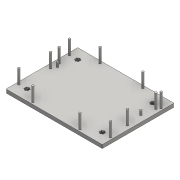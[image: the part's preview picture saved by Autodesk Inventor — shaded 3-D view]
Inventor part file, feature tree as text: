
AUTODESK INVENTOR PART (.ipt)
format: ipt  version: 2016 (Build 200138000, 138)  size: 360,448 bytes
history: native  units: mm
features: extrude x6, sketch x2, hole x2, other x2, fillet x2, pattern_linear x1
ambient origin geometry x8: Origin, YZ Plane, XZ Plane, XY Plane, X Axis, Y Axis, Z Axis, Center Point
bodies: Solid1 (feature_tree)
feature tree (15):
  sketch  "Sketch1"  dims[d9=60.0mm d10=5.0mm]
  hole  "HOLES1"  [1 undecoded]
  other  "OUTLINE1"
  other  "OUTLINE2"
  extrude  "Extrusion2"  Depth=5.0mm TaperAngle=0.0deg
  fillet  "Fillet1"  Radius=0.5mm
  extrude  "Extrusion7"  Depth=6.0mm
  fillet  "Fillet3"  Radius=3.0mm
  extrude  "Extrusion8"  Depth=6.0mm
  extrude  "Extrusion9"  Depth=6.0mm
  pattern_linear  "Rectangular Pattern2"  Spacing1=3.0mm  [1 undecoded]
  sketch  "Sketch8"  dims[d11=5.0mm d14=5.0mm d15=0.0mm d36=0.5mm d44=3.0mm d45=3.0mm d46=3.0mm d47=3.0mm d48=3.0mm d49=3.0mm d50=3.0mm d51=3.0mm d52=10.0mm d53=10.0mm d56=10.0mm d57=10.0mm d58=0.0mm d59=0.5mm d62=5.0mm d63=2.85mm d64=1.0mm d65=60.0mm d67=360.0deg d69=2.3mm d70=0.0mm d71=5.0mm d72=10.0mm d73=0.0mm d74=20.0mm d76=72.0mm d77=20.0mm d79=107.0mm d80=3.0mm d81=30.0mm d82=1.8mm d83=3.0mm d84=30.0mm d85=1.8mm d86=3.0mm d87=3.0mm d88=3.0mm d90=3.0mm d91=3.0mm d92=3.0mm d93=3.0mm d94=3.0mm d95=3.0mm d96=3.0mm d97=1.8mm d98=10.0mm d99=1.8mm d100=10.0mm d101=1.8mm d102=5.0mm d103=1.8mm d104=5.0mm d105=3.0mm d106=1.8mm d107=33.0mm d108=1.8mm d109=5.0mm d110=1.8mm d111=5.0mm d112=1.8mm d113=10.0mm d114=1.8mm d115=30.0mm d116=1.8mm d117=30.0mm d118=1.8mm d119=10.0mm d120=3.0mm d121=1.8mm d122=33.0mm d123=3.0mm d124=6.0mm d125=4.0mm d126=2.0mm d127=90.0deg d128=8.0mm d129=20.594885mm d130=20.0mm d131=0.0mm d132=6.0mm d133=0.0mm]
  hole  "Hole1"  [1 undecoded]
  extrude  "Extrusion10"  Depth=6.0mm
  extrude  "Extrusion11"  Depth=6.0mm
note: 3 required parameter values undecoded (feature->parameter linkage not recoverable at this tier; creation-order binding heuristic only, values carry confidence <= 0.55)
